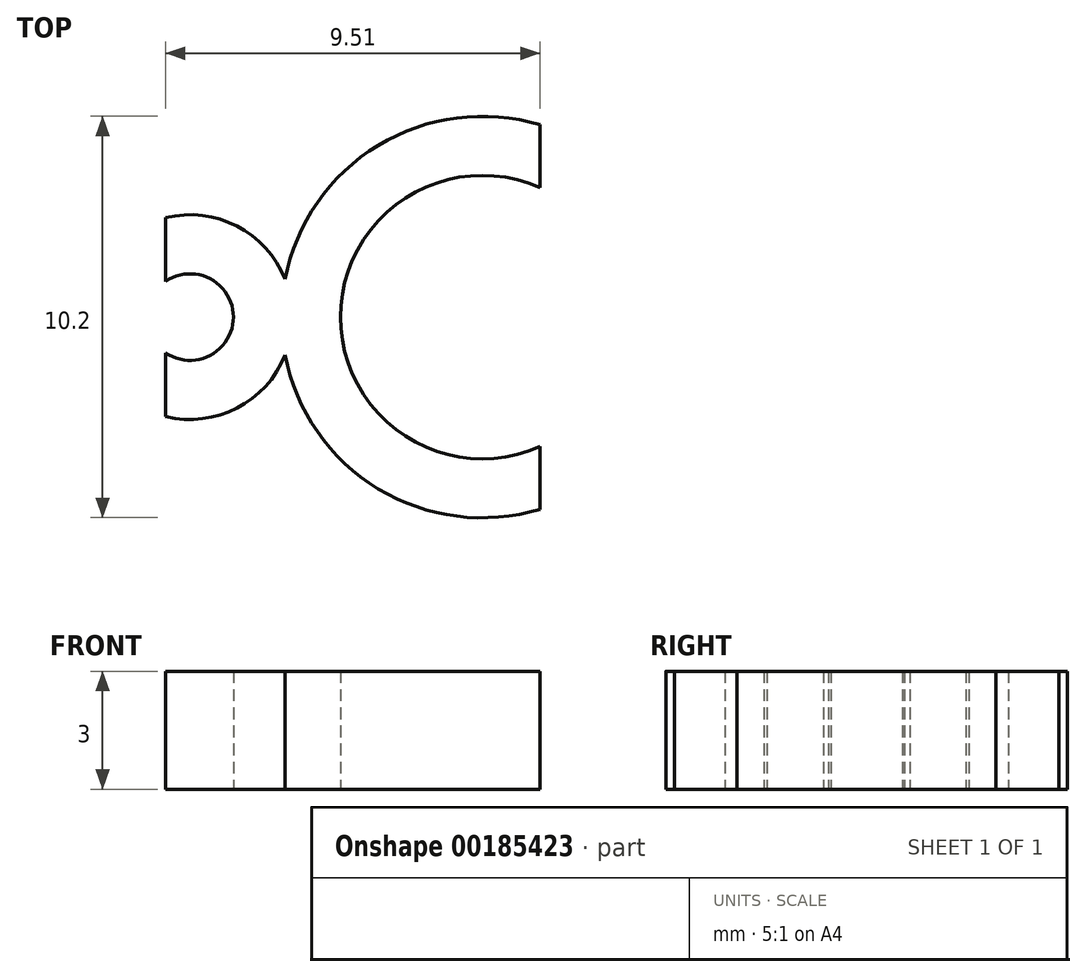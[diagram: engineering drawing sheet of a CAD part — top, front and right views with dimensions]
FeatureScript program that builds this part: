
annotation { "Feature Type Name" : "Feature", "Feature Type Description" : "" }
export const myFeature = defineFeature(function(context is Context, id is Id, definition is map)
    precondition{}
    {
        {
            var Q0;
            Q0=qCreatedBy(makeId("Top.planeOp"),FACE);
            var sketch = newSketch(context, id + "F0", { "sketchPlane" : qUnion([Q0])});
            skArc(sketch, "E0", {"start": v(2.77, 4.67) * mm, "mid": v(-2.3, 1.38) * mm, "end": v(2.77, -1.91) * mm});
            skArc(sketch, "E1", {"start": v(2.77, 6.26) * mm, "mid": v(-1.34, 5.74) * mm, "end": v(-3.7, 2.34) * mm});
            skLineSegment(sketch, "E2", {"start": v(2.77, -1.91) * mm, "end": v(2.77, -3.5) * mm});
            skLineSegment(sketch, "E3", {"start": v(2.77, 4.67) * mm, "end": v(2.77, 6.26) * mm});
            skArc(sketch, "E4", {"start": v(-6.74, 0.47) * mm, "mid": v(-5.02, 1.38) * mm, "end": v(-6.74, 2.29) * mm});
            skArc(sketch, "E5", {"start": v(-6.74, -1.15) * mm, "mid": v(-4.93, -0.94) * mm, "end": v(-3.7, 0.41) * mm});
            skLineSegment(sketch, "E6", {"start": v(-6.74, 2.29) * mm, "end": v(-6.74, 3.9) * mm});
            skLineSegment(sketch, "E7", {"start": v(-6.74, 0.47) * mm, "end": v(-6.74, -1.15) * mm});
            skArc(sketch, "E8.trimOffspring", {"start": v(-3.7, 0.41) * mm, "mid": v(-1.34, -2.98) * mm, "end": v(2.77, -3.5) * mm});
            skArc(sketch, "E9.trimOffspring", {"start": v(-3.7, 2.34) * mm, "mid": v(-4.93, 3.69) * mm, "end": v(-6.74, 3.9) * mm});
            skSolve(sketch);
        }
        {
            var Q0;
            Q0=makeQuery(id+"F0.imprint","IMPRINT",FACE,{"disambiguationData":[TD([[makeQuery(id+"F0.imprint","IMPRINT",EDGE,{"derivedFrom":sQuery(id+"F0.wireOp",EDGE,"E0")}),-1.0]])]});
            extrude(context, id + "F1", {"entities" : qUnion([Q0]), "depth" : 3 * mm});
        }
    });
